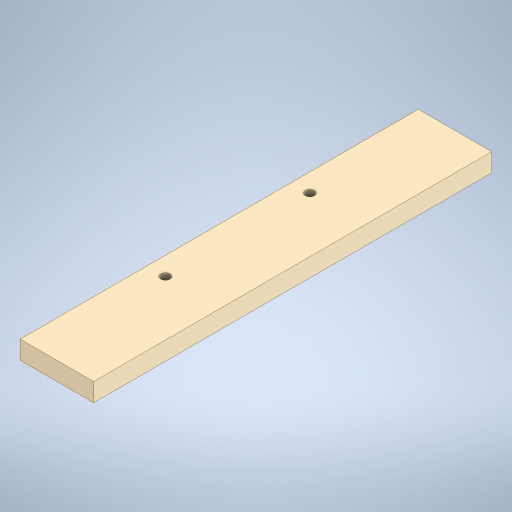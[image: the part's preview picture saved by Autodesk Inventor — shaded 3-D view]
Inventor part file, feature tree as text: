
AUTODESK INVENTOR PART (.ipt)
format: ipt  version: 2024 (Build 280153000, 153)  size: 238,592 bytes
history: native  units: in
note: dims shown in document units (in); Inventor stores cm internally (conversion verified against a paired STEP export)
features: extrude x2, sketch x2
ambient origin geometry x8: Origin, YZ Plane, XZ Plane, XY Plane, X Axis, Y Axis, Z Axis, Center Point
bodies: Solid1 (feature_tree)
feature tree (4):
  extrude  "Extrusion1"  Depth=10.8425in
  extrude  "Extrusion2"  Depth=0.5in
  sketch  "Sketch1"  dims[d0=2.0in d1=10.8425in]
  sketch  "Sketch2"  dims[d2=0.5in d3=0.0in d4=3.4528in d5=3.937in d6=0.25in d7=1.5in d8=0.5in d9=0.0in]
